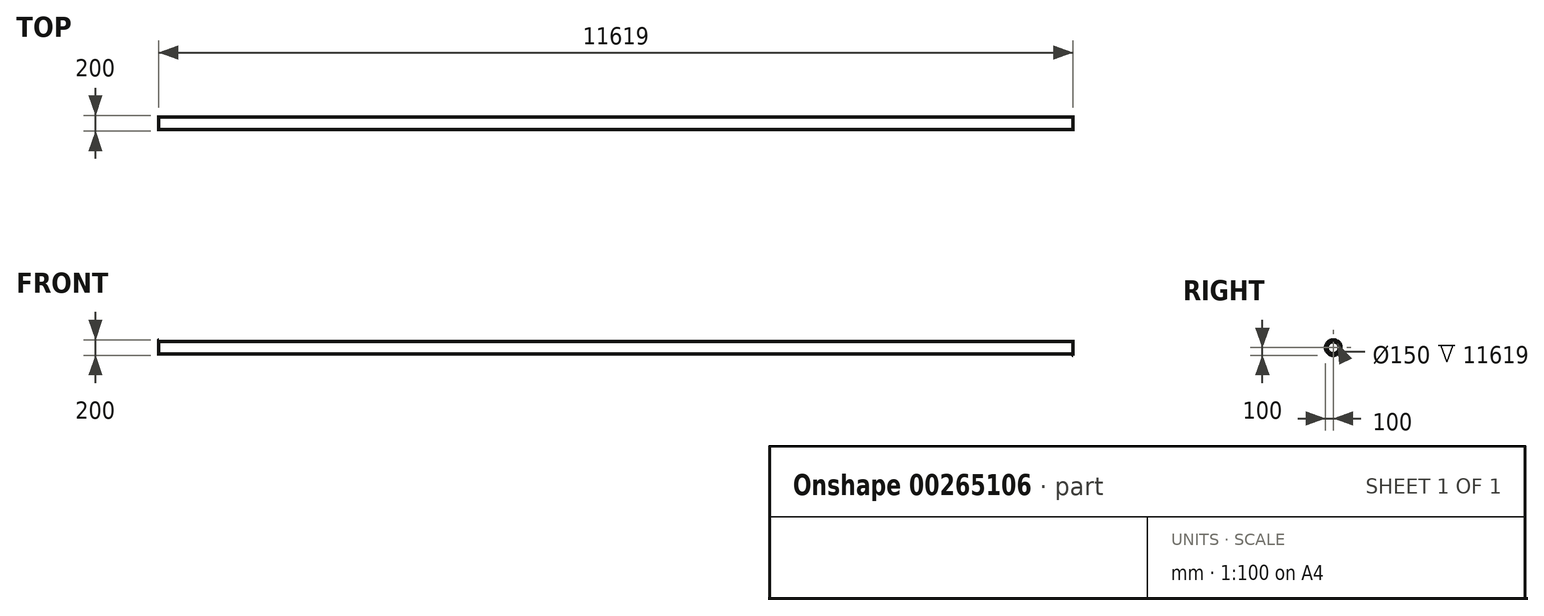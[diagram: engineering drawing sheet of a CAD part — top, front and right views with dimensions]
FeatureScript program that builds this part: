
annotation { "Feature Type Name" : "Feature", "Feature Type Description" : "" }
export const myFeature = defineFeature(function(context is Context, id is Id, definition is map)
    precondition{}
    {
        {
            var Q0;
            Q0=qCreatedBy(makeId("Front.planeOp"),FACE);
            var sketch = newSketch(context, id + "F0", { "sketchPlane" : qUnion([Q0])});
            skLineSegment(sketch, "E0", {"start": v(0, 0) * mm, "end": v(-11609, 0) * mm, "construction": true});
            skLineSegment(sketch, "E1.bottom", {"start": v(0, 75) * mm, "end": v(-11609, 75) * mm});
            skLineSegment(sketch, "E1.top", {"start": v(0, 78) * mm, "end": v(-11609, 78) * mm});
            skLineSegment(sketch, "E1.left", {"start": v(0, 75) * mm, "end": v(0, 78) * mm});
            skLineSegment(sketch, "E1.right", {"start": v(-11609, 75) * mm, "end": v(-11609, 78) * mm});
            skSolve(sketch);
        }
        {
            var Q0;
            Q0=makeQuery(id+"F0.imprint","IMPRINT",FACE,{"disambiguationData":[TD([[makeQuery(id+"F0.imprint","IMPRINT",EDGE,{"derivedFrom":sQuery(id+"F0.wireOp",EDGE,"E1.bottom")}),-1.0]])]});
            var Q1;
            Q1=sQuery(id+"F0.wireOp",EDGE,"E0");
            revolve(context, id + "F1", {"entities" : qUnion([Q0]), "axis" : qUnion([Q1]), "revolveType" : RevolveType.FULL});
        }
        {
            var Q0;
            Q0=makeQuery(id+"F1.opRevolve","SWEPT_FACE",FACE,{"disambiguationData":[OSD([sQuery(id+"F0.wireOp",EDGE,"E1.right")])]});
            var sketch = newSketch(context, id + "F2", { "sketchPlane" : qUnion([Q0])});
            skCircle(sketch, "E2", {"center": v(0, 0) * mm, "radius": 100 * mm});
            skCircle(sketch, "E3", {"center": v(0, 0) * mm, "radius": 75 * mm});
            skSolve(sketch);
        }
        {
            var Q0;
            Q0 = qSketchRegion(id + "F2", true);
            extrude(context, id + "F3", {"entities" : qUnion([Q0]), "operationType" : NewBodyOperationType.ADD, "depth" : 5 * mm});
        }
        {
            var Q0;
            Q0=makeQuery(id+"F1.opRevolve","SWEPT_FACE",FACE,{"disambiguationData":[OSD([sQuery(id+"F0.wireOp",EDGE,"E1.left")])]});
            var sketch = newSketch(context, id + "F4", { "sketchPlane" : qUnion([Q0])});
            skCircle(sketch, "E4", {"center": v(0, 0) * mm, "radius": 100 * mm});
            skCircle(sketch, "E5", {"center": v(0, 0) * mm, "radius": 75 * mm});
            skSolve(sketch);
        }
        {
            var Q0;
            Q0 = qSketchRegion(id + "F4", true);
            extrude(context, id + "F5", {"entities" : qUnion([Q0]), "operationType" : NewBodyOperationType.ADD, "depth" : 5 * mm});
        }
    });
